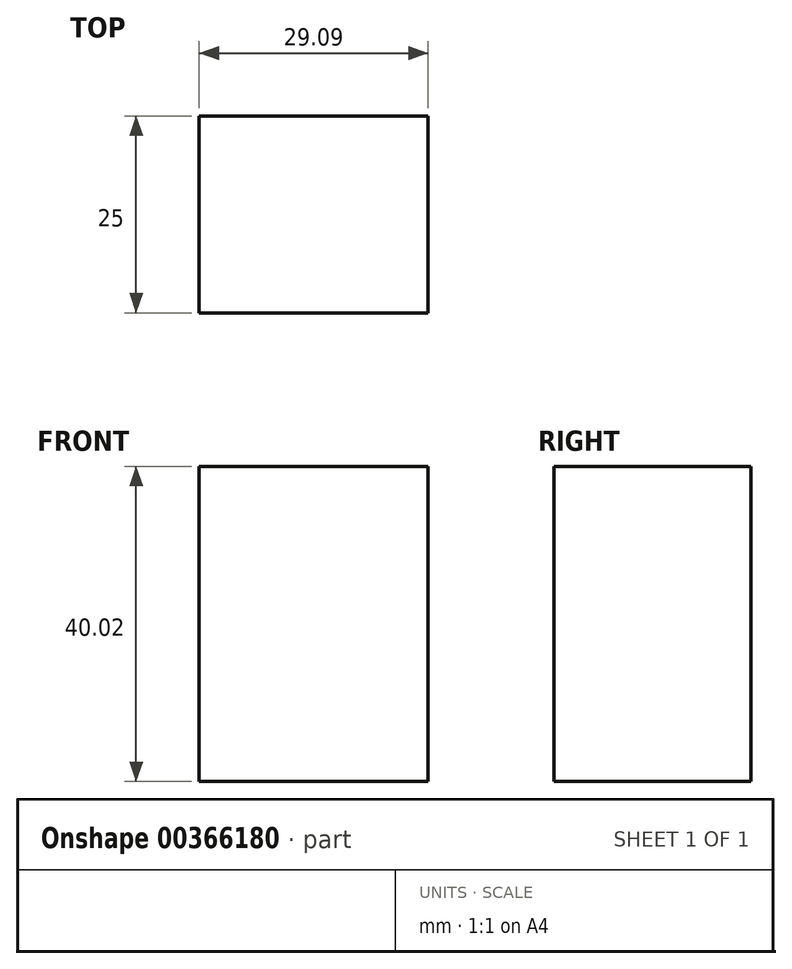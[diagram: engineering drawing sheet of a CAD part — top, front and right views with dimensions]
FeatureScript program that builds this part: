
annotation { "Feature Type Name" : "Feature", "Feature Type Description" : "" }
export const myFeature = defineFeature(function(context is Context, id is Id, definition is map)
    precondition{}
    {
        {
            var Q0;
            Q0=qCreatedBy(makeId("Front.planeOp"),FACE);
            var sketch = newSketch(context, id + "F0", { "sketchPlane" : qUnion([Q0])});
            skLineSegment(sketch, "E0.bottom", {"start": v(27.19, 123.86) * mm, "end": v(56.28, 123.86) * mm});
            skLineSegment(sketch, "E0.top", {"start": v(27.19, 83.84) * mm, "end": v(56.28, 83.84) * mm});
            skLineSegment(sketch, "E0.left", {"start": v(27.19, 123.86) * mm, "end": v(27.19, 83.84) * mm});
            skLineSegment(sketch, "E0.right", {"start": v(56.28, 123.86) * mm, "end": v(56.28, 83.84) * mm});
            skSolve(sketch);
        }
        {
            var Q0;
            Q0=makeQuery(id+"F0.imprint","IMPRINT",FACE,{"disambiguationData":[TD([[makeQuery(id+"F0.imprint","IMPRINT",EDGE,{"derivedFrom":sQuery(id+"F0.wireOp",EDGE,"E0.bottom")}),-1.0]])]});
            extrude(context, id + "F1", {"entities" : qUnion([Q0]), "depth" : 25 * mm});
        }
    });
